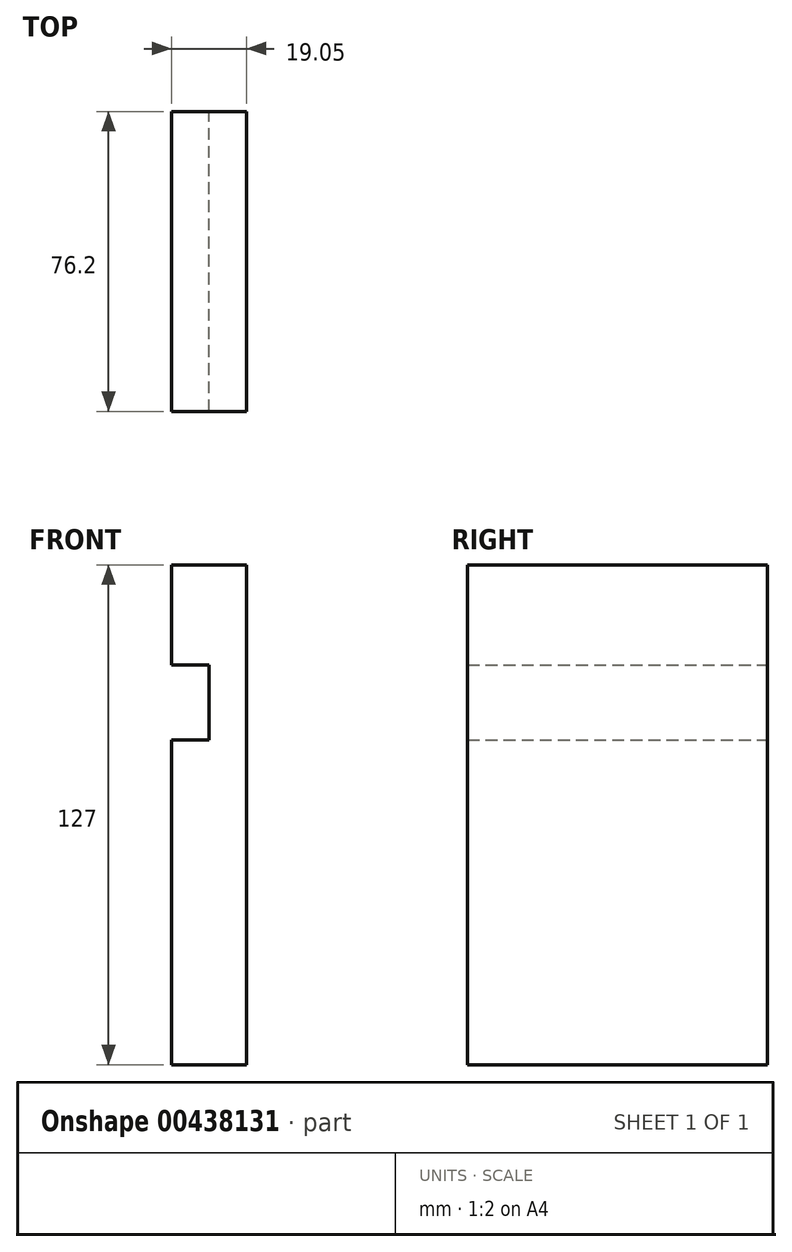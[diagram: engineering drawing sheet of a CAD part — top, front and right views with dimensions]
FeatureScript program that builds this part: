
annotation { "Feature Type Name" : "Feature", "Feature Type Description" : "" }
export const myFeature = defineFeature(function(context is Context, id is Id, definition is map)
    precondition{}
    {
        {
            var Q0;
            Q0=qCreatedBy(makeId("Front.planeOp"),FACE);
            var sketch = newSketch(context, id + "F0", { "sketchPlane" : qUnion([Q0])});
            skLineSegment(sketch, "E0", {"start": v(24.82, -71.6) * mm, "end": v(43.87, -71.6) * mm});
            skLineSegment(sketch, "E1", {"start": v(43.87, -71.6) * mm, "end": v(43.87, 55.4) * mm});
            skLineSegment(sketch, "E2", {"start": v(43.87, 55.4) * mm, "end": v(24.82, 55.4) * mm});
            skLineSegment(sketch, "E3", {"start": v(24.82, 55.4) * mm, "end": v(24.82, 30) * mm});
            skLineSegment(sketch, "E4", {"start": v(24.82, 30) * mm, "end": v(34.35, 30) * mm});
            skLineSegment(sketch, "E5", {"start": v(34.35, 30) * mm, "end": v(34.35, 10.94) * mm});
            skLineSegment(sketch, "E6", {"start": v(34.35, 10.94) * mm, "end": v(24.82, 10.94) * mm});
            skLineSegment(sketch, "E7", {"start": v(24.82, 10.94) * mm, "end": v(24.82, -71.6) * mm});
            skSolve(sketch);
        }
        {
            var Q0;
            Q0=qSketchRegion(id+"F0",true);
            extrude(context, id + "F1", {"entities" : qUnion([Q0]), "depth" : 76.2 * mm});
        }
    });
